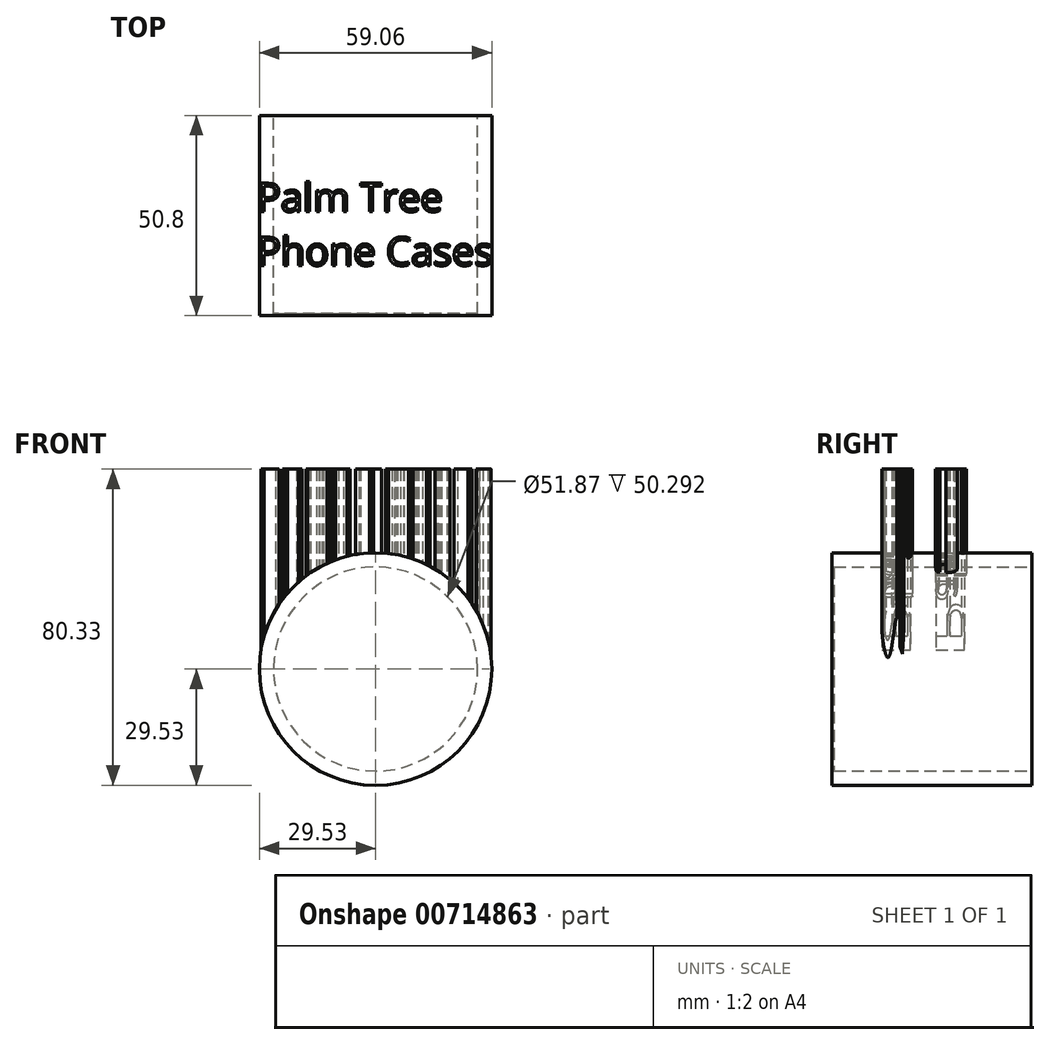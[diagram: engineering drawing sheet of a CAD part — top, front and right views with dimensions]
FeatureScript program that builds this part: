
annotation { "Feature Type Name" : "Feature", "Feature Type Description" : "" }
export const myFeature = defineFeature(function(context is Context, id is Id, definition is map)
    precondition{}
    {
        {
            var Q0;
            Q0=qCreatedBy(makeId("Front.planeOp"),FACE);
            var sketch = newSketch(context, id + "F0", { "sketchPlane" : qUnion([Q0])});
            skCircle(sketch, "E0", {"center": v(0, 0) * mm, "radius": 29.53 * mm});
            skSolve(sketch);
        }
        {
            var Q0;
            Q0=makeQuery(id+"F0.imprint","IMPRINT",FACE,{"disambiguationData":[TD([[makeQuery(id+"F0.imprint","IMPRINT",EDGE,{"derivedFrom":sQuery(id+"F0.wireOp",EDGE,"E0")}),1.0]])]});
            extrude(context, id + "F1", {"entities" : qUnion([Q0]), "depth" : 50.8 * mm, "offsetDistance" : 25.4 * mm});
        }
        {
            var Q0;
            Q0=qCreatedBy(makeId("Top.planeOp"),FACE);
            var sketch = newSketch(context, id + "F2", { "sketchPlane" : qUnion([Q0])});
            skText(sketch, "E1", { "text": "Palm Tree \nPhone Cases", "fontName": "OpenSans-Regular.ttf"});
            const initialGuessF2  = {"E1": [-0.03013, -0.02438, 1, 0, 0.00725]};
            skSetInitialGuess(sketch, initialGuessF2);
            skSolve(sketch);
        }
        {
            var Q0;
            Q0 = qSketchRegion(id + "F2", true);
            extrude(context, id + "F3", {"entities" : qUnion([Q0]), "operationType" : NewBodyOperationType.ADD, "depth" : 50.8 * mm, "offsetDistance" : 25.4 * mm});
        }
        {
            var Q0;
            Q0=makeQuery(id+"F1.opExtrude","CAP_FACE",FACE,{"disambiguationData":[OSD([sQuery(id+"F0.wireOp",EDGE,"E0")])],"isStart":true});
            var sketch = newSketch(context, id + "F4", { "sketchPlane" : qUnion([Q0])});
            skCircle(sketch, "E2", {"center": v(0, 0) * mm, "radius": 25.93 * mm});
            skSolve(sketch);
        }
        {
            var Q0;
            Q0=makeQuery(id+"F4.imprint","IMPRINT",FACE,{"disambiguationData":[TD([[makeQuery(id+"F4.imprint","IMPRINT",EDGE,{"derivedFrom":sQuery(id+"F4.wireOp",EDGE,"E2")}),1.0]])]});
            extrude(context, id + "F5", {"entities" : qUnion([Q0]), "operationType" : NewBodyOperationType.REMOVE, "oppositeDirection" : true, "depth" : 50.3 * mm, "offsetDistance" : 25.4 * mm});
        }
    });
